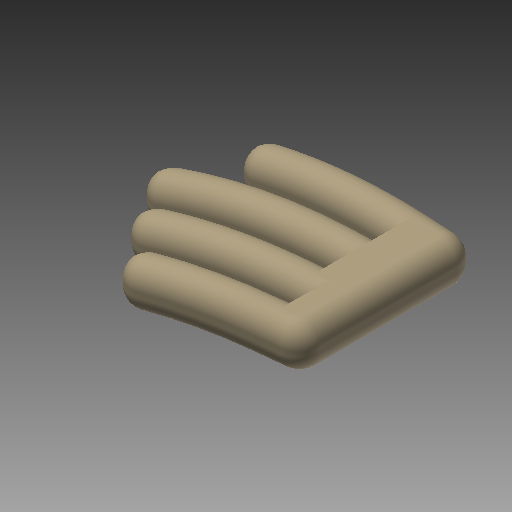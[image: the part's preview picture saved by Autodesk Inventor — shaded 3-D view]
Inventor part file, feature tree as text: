
AUTODESK INVENTOR PART (.ipt)
format: ipt  version: 2022 (Build 260153000, 153)  size: 642,048 bytes
history: native  units: mm (DEFAULTED — no unit token found)
features: fillet x3, other x2, extrude x2, sketch x2, projected_geometry x2, plane x1
ambient origin geometry x8: Origin, YZ Plane, XZ Plane, XY Plane, X Axis, Y Axis, Z Axis, Center Point
bodies: Solid1 (feature_tree)
feature tree (12):
  other  "iMandy - 2D BODY"
  extrude  "Extrusion1"  Depth=10.0mm
  extrude  "Extrusion2"  Depth=1.80086mm
  fillet  "Fillet1"  Radius=90.043mm
  fillet  "Fillet3"  Radius=54.0258mm
  fillet  "Fillet4"  Radius=90.043mm
  other  "Work Axis1"
  plane  "Work Plane1"
  sketch  "Sketch1"  dims[d1=10.0mm d16=0.523599mm]
  sketch  "Sketch2"  dims[d17=0.523599mm d18=3.490659mm d19=90.043mm d20=54.0258mm d22=90.043mm d23=4.50215mm d24=36.0172mm d25=0.0mm d26=9.0043mm d28=18.0086mm d29=0.0mm d30=7.878763mm d31=1.80086mm d32=85.779821mm d33=75.057343mm]
  projected_geometry  "Projected Loop1"
  projected_geometry  "Projected Loop2"
